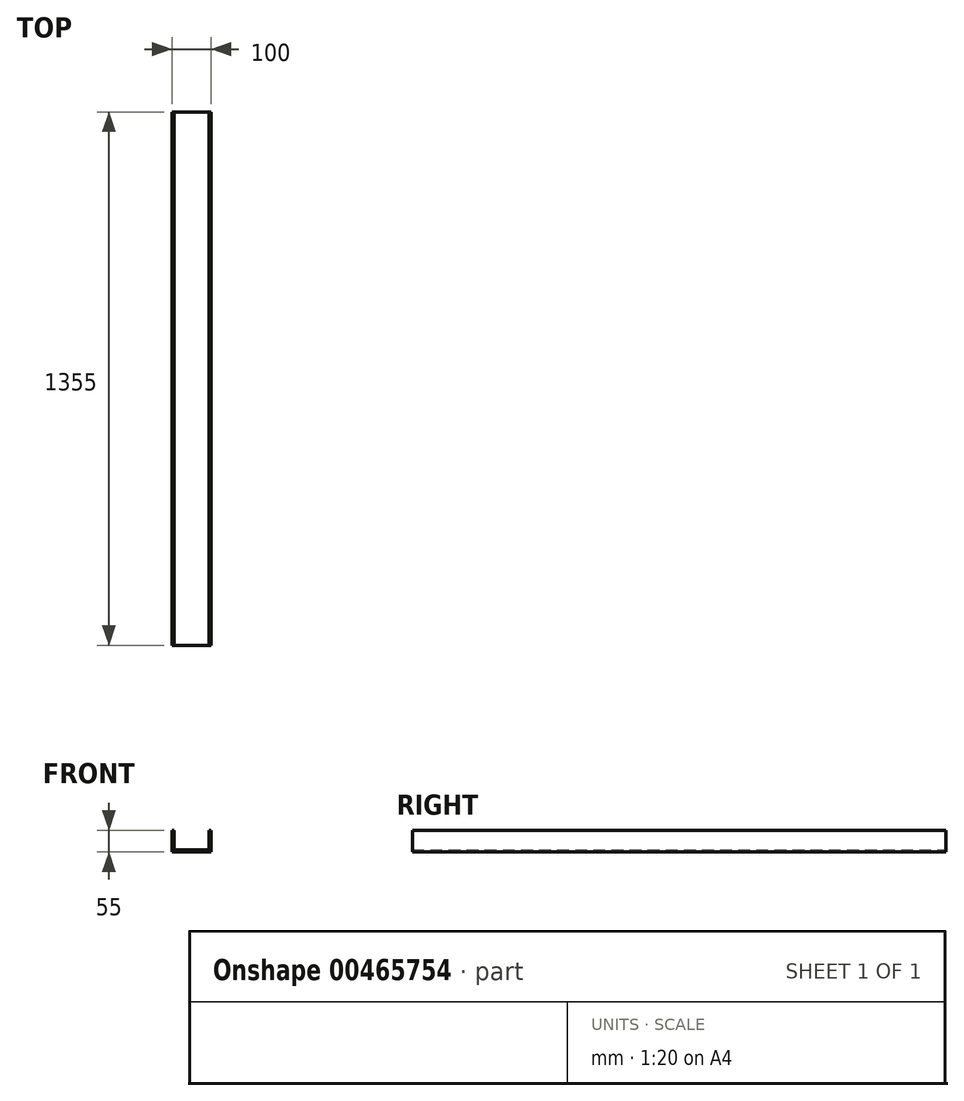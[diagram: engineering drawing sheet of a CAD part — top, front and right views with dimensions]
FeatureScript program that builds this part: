
annotation { "Feature Type Name" : "Feature", "Feature Type Description" : "" }
export const myFeature = defineFeature(function(context is Context, id is Id, definition is map)
    precondition{}
    {
        {
            var Q0;
            Q0=qCreatedBy(makeId("Front.planeOp"),FACE);
            var sketch = newSketch(context, id + "F0", { "sketchPlane" : qUnion([Q0])});
            skLineSegment(sketch, "E0", {"start": v(-7.7, -3.13) * mm, "end": v(-7.7, 51.87) * mm});
            skLineSegment(sketch, "E1", {"start": v(-7.7, -3.13) * mm, "end": v(92.3, -3.13) * mm});
            skLineSegment(sketch, "E2", {"start": v(92.3, -3.13) * mm, "end": v(92.3, 51.87) * mm});
            skLineSegment(sketch, "E3", {"start": v(92.3, 51.87) * mm, "end": v(87.3, 51.87) * mm});
            skLineSegment(sketch, "E4", {"start": v(87.3, 51.87) * mm, "end": v(87.3, 1.87) * mm});
            skLineSegment(sketch, "E5", {"start": v(-7.7, 51.87) * mm, "end": v(-2.7, 51.87) * mm});
            skLineSegment(sketch, "E6", {"start": v(-2.7, 51.87) * mm, "end": v(-2.7, 1.87) * mm});
            skLineSegment(sketch, "E7", {"start": v(-2.7, 1.87) * mm, "end": v(87.3, 1.87) * mm});
            skSolve(sketch);
        }
        {
            var Q0;
            Q0=makeQuery(id+"F0.imprint","IMPRINT",FACE,{"disambiguationData":[TD([[makeQuery(id+"F0.imprint","IMPRINT",EDGE,{"derivedFrom":sQuery(id+"F0.wireOp",EDGE,"E0")}),-1.0]])]});
            extrude(context, id + "F1", {"entities" : qUnion([Q0]), "depth" : 1355 * mm, "offsetDistance" : 25 * mm});
        }
    });
